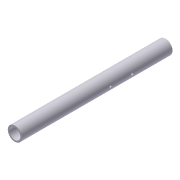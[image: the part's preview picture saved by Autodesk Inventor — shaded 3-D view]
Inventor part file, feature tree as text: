
AUTODESK INVENTOR PART (.ipt)
format: ipt  version: 2012 (Build 160160000, 160)  size: 87,040 bytes
history: native  units: in
note: dims shown in document units (in); Inventor stores cm internally (conversion verified against a paired STEP export)
features: extrude x2, sketch x2, plane x1, pattern_linear x1, other x1, projected_geometry x1
ambient origin geometry x8: Origin, YZ Plane, XZ Plane, XY Plane, X Axis, Y Axis, Z Axis, Center Point
bodies: Solid1 (feature_tree)
feature tree (8):
  extrude  "Extrusion1"  Depth=1.3125in
  plane  "Work Plane1"
  extrude  "Extrusion2"  TaperAngle=0.0deg  [1 undecoded]
  pattern_linear  "Rectangular Pattern1"  Spacing1=0.191in  [1 undecoded]
  sketch  "Sketch1"  dims[d0=1.0313in d1=1.3125in]
  other  "Work Axis1"
  sketch  "Sketch2"  dims[d2=14.0in d3=0.0in d4=0.0in d5=0.191in d6=8.25in d7=15.0in d8=0.0in d9=0.7874in d11=2.0in]
  projected_geometry  "Projected Loop1"
note: 2 required parameter values undecoded (feature->parameter linkage not recoverable at this tier; creation-order binding heuristic only, values carry confidence <= 0.55)
